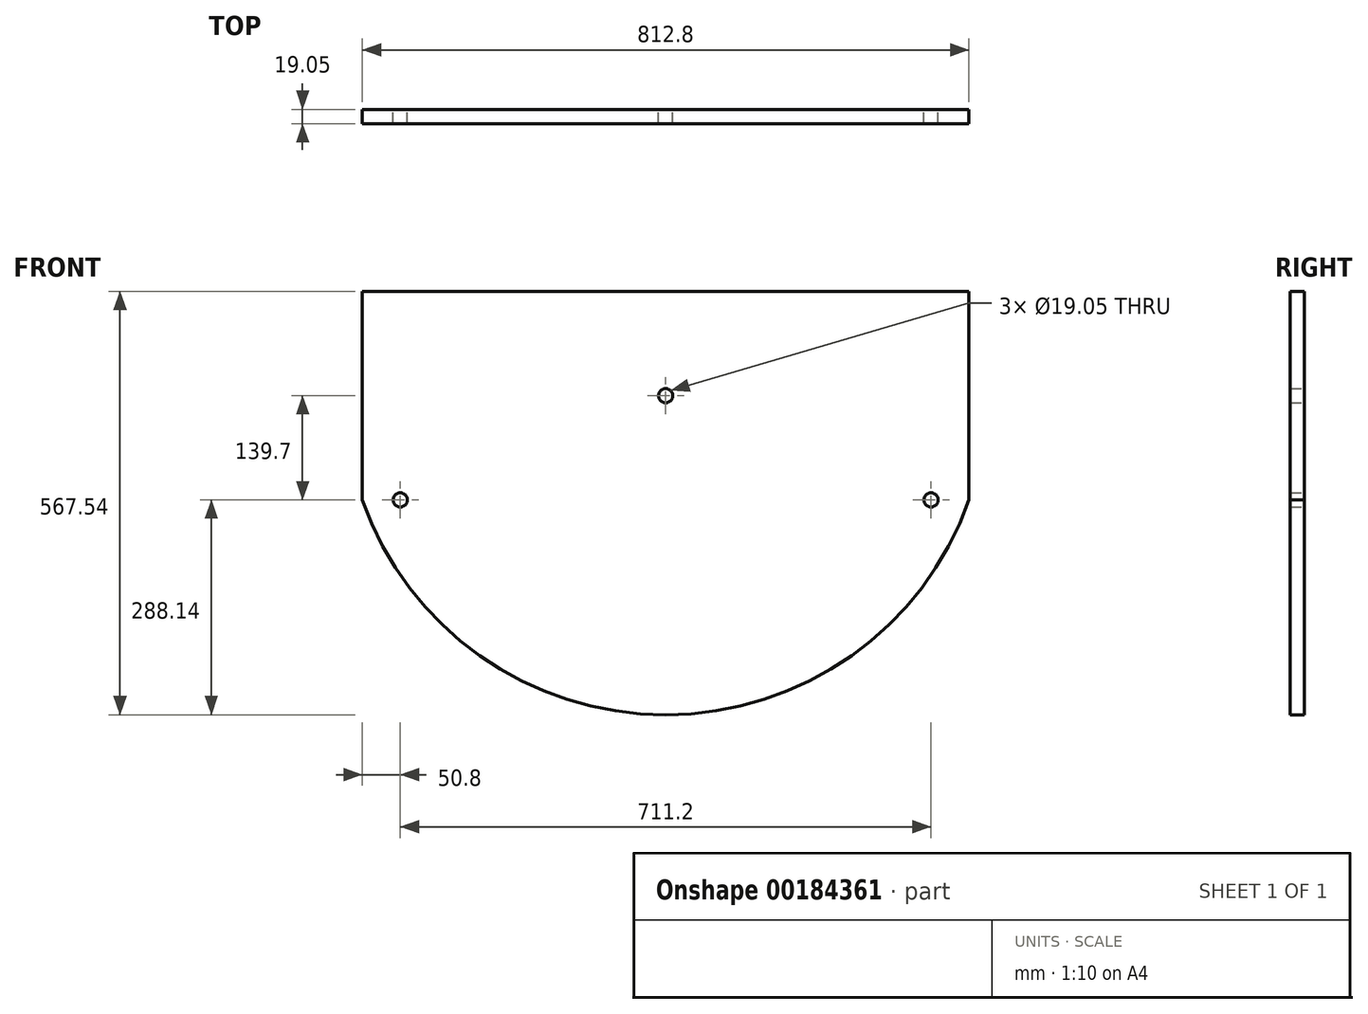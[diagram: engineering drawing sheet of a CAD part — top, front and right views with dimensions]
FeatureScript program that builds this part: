
annotation { "Feature Type Name" : "Feature", "Feature Type Description" : "" }
export const myFeature = defineFeature(function(context is Context, id is Id, definition is map)
    precondition{}
    {
        {
            var Q0;
            Q0=qCreatedBy(makeId("Front.planeOp"),FACE);
            var sketch = newSketch(context, id + "F0", { "sketchPlane" : qUnion([Q0])});
            skLineSegment(sketch, "E0", {"start": v(-406.4, 139.7) * mm, "end": v(406.4, 139.7) * mm});
            skLineSegment(sketch, "E1", {"start": v(-406.4, 139.7) * mm, "end": v(-406.4, -139.7) * mm});
            skLineSegment(sketch, "E2", {"start": v(406.4, 139.7) * mm, "end": v(406.4, -139.7) * mm});
            skArc(sketch, "E3", {"start": v(-406.4, -139.7) * mm, "mid": v(0, -427.84) * mm, "end": v(406.4, -139.7) * mm});
            skCircle(sketch, "E4", {"center": v(-355.6, -139.7) * mm, "radius": 9.53 * mm});
            skCircle(sketch, "E5", {"center": v(355.6, -139.7) * mm, "radius": 9.53 * mm});
            skCircle(sketch, "E6", {"center": v(0, 0) * mm, "radius": 9.53 * mm});
            skSolve(sketch);
        }
        {
            var Q0;
            Q0=makeQuery(id+"F0.imprint","IMPRINT",FACE,{"disambiguationData":[TD([[makeQuery(id+"F0.imprint","IMPRINT",EDGE,{"derivedFrom":sQuery(id+"F0.wireOp",EDGE,"E0")}),-1.0]])]});
            extrude(context, id + "F1", {"entities" : qUnion([Q0]), "depth" : 19.05 * mm});
        }
    });
